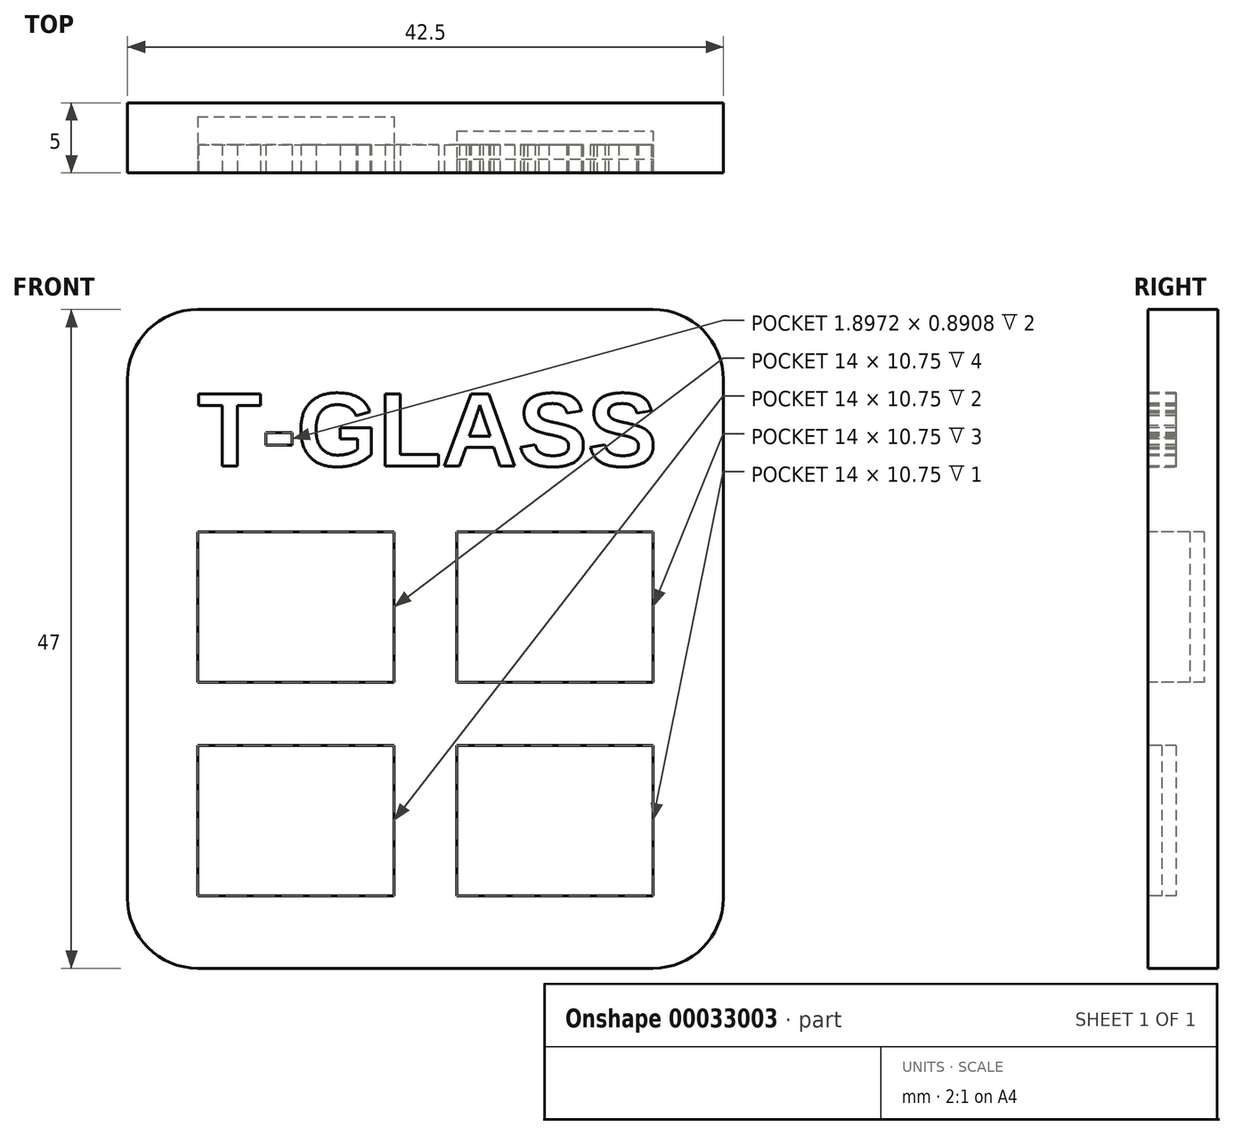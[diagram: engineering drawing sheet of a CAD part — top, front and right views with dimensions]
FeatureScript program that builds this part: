
annotation { "Feature Type Name" : "Feature", "Feature Type Description" : "" }
export const myFeature = defineFeature(function(context is Context, id is Id, definition is map)
    precondition{}
    {
        {
            var Q0;
            Q0=qCreatedBy(makeId("Front.planeOp"),FACE);
            var sketch = newSketch(context, id + "F0", { "sketchPlane" : qUnion([Q0])});
            skLineSegment(sketch, "E0.rect.bottom", {"start": v(16.25, -23.5) * mm, "end": v(-16.25, -23.5) * mm});
            skLineSegment(sketch, "E0.rect.top", {"start": v(16.25, 23.5) * mm, "end": v(-16.25, 23.5) * mm});
            skLineSegment(sketch, "E0.rect.left", {"start": v(21.25, -18.5) * mm, "end": v(21.25, 18.5) * mm});
            skLineSegment(sketch, "E0.rect.right", {"start": v(-21.25, -18.5) * mm, "end": v(-21.25, 18.5) * mm});
            skPoint(sketch, "E0.rect.middle", {"position": v(0, 0) * mm});
            skPoint(sketch, "E1.visualSharp", {"position": v(-21.25, 23.5) * mm});
            skArc(sketch, "E1.filletArc", {"start": v(-16.25, 23.5) * mm, "mid": v(-19.79, 22.04) * mm, "end": v(-21.25, 18.5) * mm});
            skPoint(sketch, "E2.visualSharp", {"position": v(-21.25, -23.5) * mm});
            skArc(sketch, "E2.filletArc", {"start": v(-21.25, -18.5) * mm, "mid": v(-19.79, -22.04) * mm, "end": v(-16.25, -23.5) * mm});
            skPoint(sketch, "E3.visualSharp", {"position": v(21.25, 23.5) * mm});
            skArc(sketch, "E3.filletArc", {"start": v(21.25, 18.5) * mm, "mid": v(19.79, 22.04) * mm, "end": v(16.25, 23.5) * mm});
            skPoint(sketch, "E4.visualSharp", {"position": v(21.25, -23.5) * mm});
            skArc(sketch, "E4.filletArc", {"start": v(16.25, -23.5) * mm, "mid": v(19.79, -22.04) * mm, "end": v(21.25, -18.5) * mm});
            skSolve(sketch);
        }
        {
            var Q0;
            Q0 = qSketchRegion(id + "F0", true);
            extrude(context, id + "F1", {"entities" : qUnion([Q0]), "depth" : 5 * mm});
        }
        {
            var Q0;
            Q0=makeQuery(id+"F1.opExtrude","CAP_FACE",FACE,{"disambiguationData":[OSD([sQuery(id+"F0.wireOp",EDGE,"E0.rect.bottom"),sQuery(id+"F0.wireOp",EDGE,"E0.rect.top"),sQuery(id+"F0.wireOp",EDGE,"E0.rect.left"),sQuery(id+"F0.wireOp",EDGE,"E0.rect.right"),sQuery(id+"F0.wireOp",EDGE,"E1.filletArc"),sQuery(id+"F0.wireOp",EDGE,"E2.filletArc"),sQuery(id+"F0.wireOp",EDGE,"E3.filletArc"),sQuery(id+"F0.wireOp",EDGE,"E4.filletArc")])],"isStart":false});
            var sketch = newSketch(context, id + "F2", { "sketchPlane" : qUnion([Q0])});
            skText(sketch, "E5", { "text": "T-GLASS", "fontName": "Arimo-Bold.ttf"});
            const initialGuessF2  = {"E5": [-0.01625, 0.01234, 1, 0, 0.00538]};
            skSetInitialGuess(sketch, initialGuessF2);
            skSolve(sketch);
        }
        {
            var Q0;
            Q0 = qSketchRegion(id + "F2", true);
            extrude(context, id + "F3", {"entities" : qUnion([Q0]), "operationType" : NewBodyOperationType.REMOVE, "oppositeDirection" : true, "depth" : 2 * mm});
        }
        {
            var Q0;
            {var subQ0=sQuery(id+"F0.wireOp",EDGE,"E0.rect.bottom");var subQ1=sQuery(id+"F0.wireOp",EDGE,"E0.rect.top");var subQ2=sQuery(id+"F0.wireOp",EDGE,"E0.rect.left");var subQ3=sQuery(id+"F0.wireOp",EDGE,"E0.rect.right");var subQ4=sQuery(id+"F0.wireOp",EDGE,"E1.filletArc");var subQ5=sQuery(id+"F0.wireOp",EDGE,"E2.filletArc");var subQ6=sQuery(id+"F0.wireOp",EDGE,"E3.filletArc");var subQ7=sQuery(id+"F0.wireOp",EDGE,"E4.filletArc");Q0=makeQuery(id+"F3.boolean.opBoolean","SPLIT",FACE,{"disambiguationData":[TD([makeQuery(id+"F1.opExtrude","SWEPT_FACE",FACE,{"disambiguationData":[OSD([subQ0])]})])],"derivedFrom":makeQuery(id+"F1.opExtrude","CAP_FACE",FACE,{"disambiguationData":[OSD([subQ0,subQ1,subQ2,subQ3,subQ4,subQ5,subQ6,subQ7])],"isStart":false})});}
            var sketch = newSketch(context, id + "F4", { "sketchPlane" : qUnion([Q0])});
            skLineSegment(sketch, "E6", {"start": v(-6.26, -7.56) * mm, "end": v(21.25, -7.56) * mm, "construction": true});
            skLineSegment(sketch, "E7.bottom", {"start": v(-16.25, 7.65) * mm, "end": v(-2.25, 7.65) * mm});
            skLineSegment(sketch, "E7.top", {"start": v(-16.25, -3.1) * mm, "end": v(-2.25, -3.1) * mm});
            skLineSegment(sketch, "E7.left", {"start": v(-16.25, 7.65) * mm, "end": v(-16.25, -3.1) * mm});
            skLineSegment(sketch, "E7.right", {"start": v(-2.25, 7.65) * mm, "end": v(-2.25, -3.1) * mm});
            skLineSegment(sketch, "E8.0.1.0", {"start": v(-16.25, -7.6) * mm, "end": v(-2.25, -7.6) * mm});
            skLineSegment(sketch, "E8.0.1.1", {"start": v(-16.25, -7.6) * mm, "end": v(-16.25, -18.35) * mm});
            skLineSegment(sketch, "E8.0.1.2", {"start": v(-16.25, -18.35) * mm, "end": v(-2.25, -18.35) * mm});
            skLineSegment(sketch, "E8.0.1.3", {"start": v(-2.25, -7.6) * mm, "end": v(-2.25, -18.35) * mm});
            skLineSegment(sketch, "E8.1.0.0", {"start": v(2.25, 7.65) * mm, "end": v(16.25, 7.65) * mm});
            skLineSegment(sketch, "E8.1.0.1", {"start": v(2.25, 7.65) * mm, "end": v(2.25, -3.1) * mm});
            skLineSegment(sketch, "E8.1.0.2", {"start": v(2.25, -3.1) * mm, "end": v(16.25, -3.1) * mm});
            skLineSegment(sketch, "E8.1.0.3", {"start": v(16.25, 7.65) * mm, "end": v(16.25, -3.1) * mm});
            skLineSegment(sketch, "E8.1.1.0", {"start": v(2.25, -7.6) * mm, "end": v(16.25, -7.6) * mm});
            skLineSegment(sketch, "E8.1.1.1", {"start": v(2.25, -7.6) * mm, "end": v(2.25, -18.35) * mm});
            skLineSegment(sketch, "E8.1.1.2", {"start": v(2.25, -18.35) * mm, "end": v(16.25, -18.35) * mm});
            skLineSegment(sketch, "E8.1.1.3", {"start": v(16.25, -7.6) * mm, "end": v(16.25, -18.35) * mm});
            skLineSegment(sketch, "E8.direction1", {"start": v(-16.25, 7.65) * mm, "end": v(2.25, 7.65) * mm, "construction": true});
            skLineSegment(sketch, "E8.direction2", {"start": v(-16.25, 7.65) * mm, "end": v(-16.25, -7.6) * mm, "construction": true});
            skSolve(sketch);
        }
        {
            var Q0;
            Q0=makeQuery(id+"F4.imprint","IMPRINT",FACE,{"disambiguationData":[TD([[makeQuery(id+"F4.imprint","IMPRINT",EDGE,{"derivedFrom":sQuery(id+"F4.wireOp",EDGE,"E7.bottom")}),-1.0]])]});
            extrude(context, id + "F5", {"entities" : qUnion([Q0]), "operationType" : NewBodyOperationType.REMOVE, "oppositeDirection" : true, "depth" : 4 * mm});
        }
        {
            var Q0;
            Q0=makeQuery(id+"F4.imprint","IMPRINT",FACE,{"disambiguationData":[TD([[makeQuery(id+"F4.imprint","IMPRINT",EDGE,{"derivedFrom":sQuery(id+"F4.wireOp",EDGE,"E8.0.1.0")}),-1.0]])]});
            extrude(context, id + "F6", {"entities" : qUnion([Q0]), "operationType" : NewBodyOperationType.REMOVE, "oppositeDirection" : true, "depth" : 2 * mm});
        }
        {
            var Q0;
            Q0=makeQuery(id+"F4.imprint","IMPRINT",FACE,{"disambiguationData":[TD([[makeQuery(id+"F4.imprint","IMPRINT",EDGE,{"derivedFrom":sQuery(id+"F4.wireOp",EDGE,"E8.1.0.0")}),-1.0]])]});
            extrude(context, id + "F7", {"entities" : qUnion([Q0]), "operationType" : NewBodyOperationType.REMOVE, "oppositeDirection" : true, "depth" : 3 * mm});
        }
        {
            var Q0;
            Q0=makeQuery(id+"F4.imprint","IMPRINT",FACE,{"disambiguationData":[TD([[makeQuery(id+"F4.imprint","IMPRINT",EDGE,{"derivedFrom":sQuery(id+"F4.wireOp",EDGE,"E8.1.1.0")}),-1.0]])]});
            extrude(context, id + "F8", {"entities" : qUnion([Q0]), "operationType" : NewBodyOperationType.REMOVE, "oppositeDirection" : true, "depth" : 1 * mm});
        }
    });
